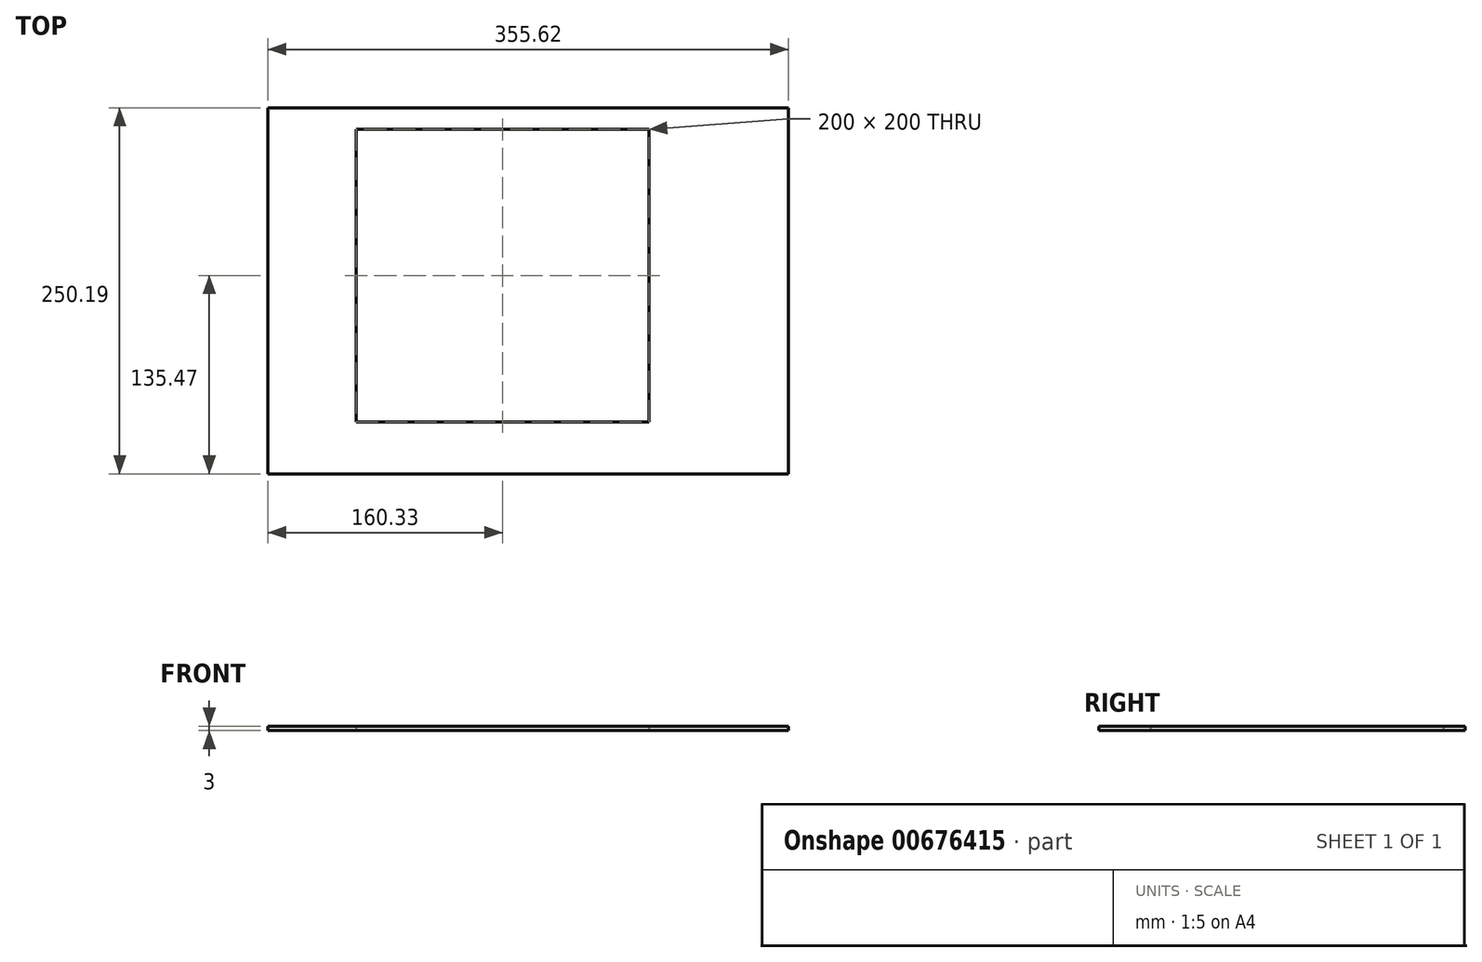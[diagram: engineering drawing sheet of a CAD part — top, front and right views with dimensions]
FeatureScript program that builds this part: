
annotation { "Feature Type Name" : "Feature", "Feature Type Description" : "" }
export const myFeature = defineFeature(function(context is Context, id is Id, definition is map)
    precondition{}
    {
        {
            var Q0;
            Q0=qCreatedBy(makeId("Top.planeOp"),FACE);
            var sketch = newSketch(context, id + "F0", { "sketchPlane" : qUnion([Q0])});
            skLineSegment(sketch, "E0.bottom", {"start": v(-160.33, 114.72) * mm, "end": v(195.29, 114.72) * mm});
            skLineSegment(sketch, "E0.top", {"start": v(-160.33, -135.47) * mm, "end": v(195.29, -135.47) * mm});
            skLineSegment(sketch, "E0.left", {"start": v(-160.33, 114.72) * mm, "end": v(-160.33, -135.47) * mm});
            skLineSegment(sketch, "E0.right", {"start": v(195.29, 114.72) * mm, "end": v(195.29, -135.47) * mm});
            skLineSegment(sketch, "E1.bottom", {"start": v(-100, 100) * mm, "end": v(100, 100) * mm});
            skLineSegment(sketch, "E1.top", {"start": v(-100, -100) * mm, "end": v(100, -100) * mm});
            skLineSegment(sketch, "E1.left", {"start": v(-100, 100) * mm, "end": v(-100, -100) * mm});
            skLineSegment(sketch, "E1.right", {"start": v(100, 100) * mm, "end": v(100, -100) * mm});
            skPoint(sketch, "E1.middle", {"position": v(0, 0) * mm});
            skSolve(sketch);
        }
        {
            var Q0;
            Q0=makeQuery(id+"F0.imprint","IMPRINT",FACE,{"disambiguationData":[TD([[makeQuery(id+"F0.imprint","IMPRINT",EDGE,{"derivedFrom":sQuery(id+"F0.wireOp",EDGE,"E0.bottom")}),-1.0]])]});
            extrude(context, id + "F1", {"entities" : qUnion([Q0]), "depth" : 3 * mm, "offsetDistance" : 25 * mm});
        }
    });
